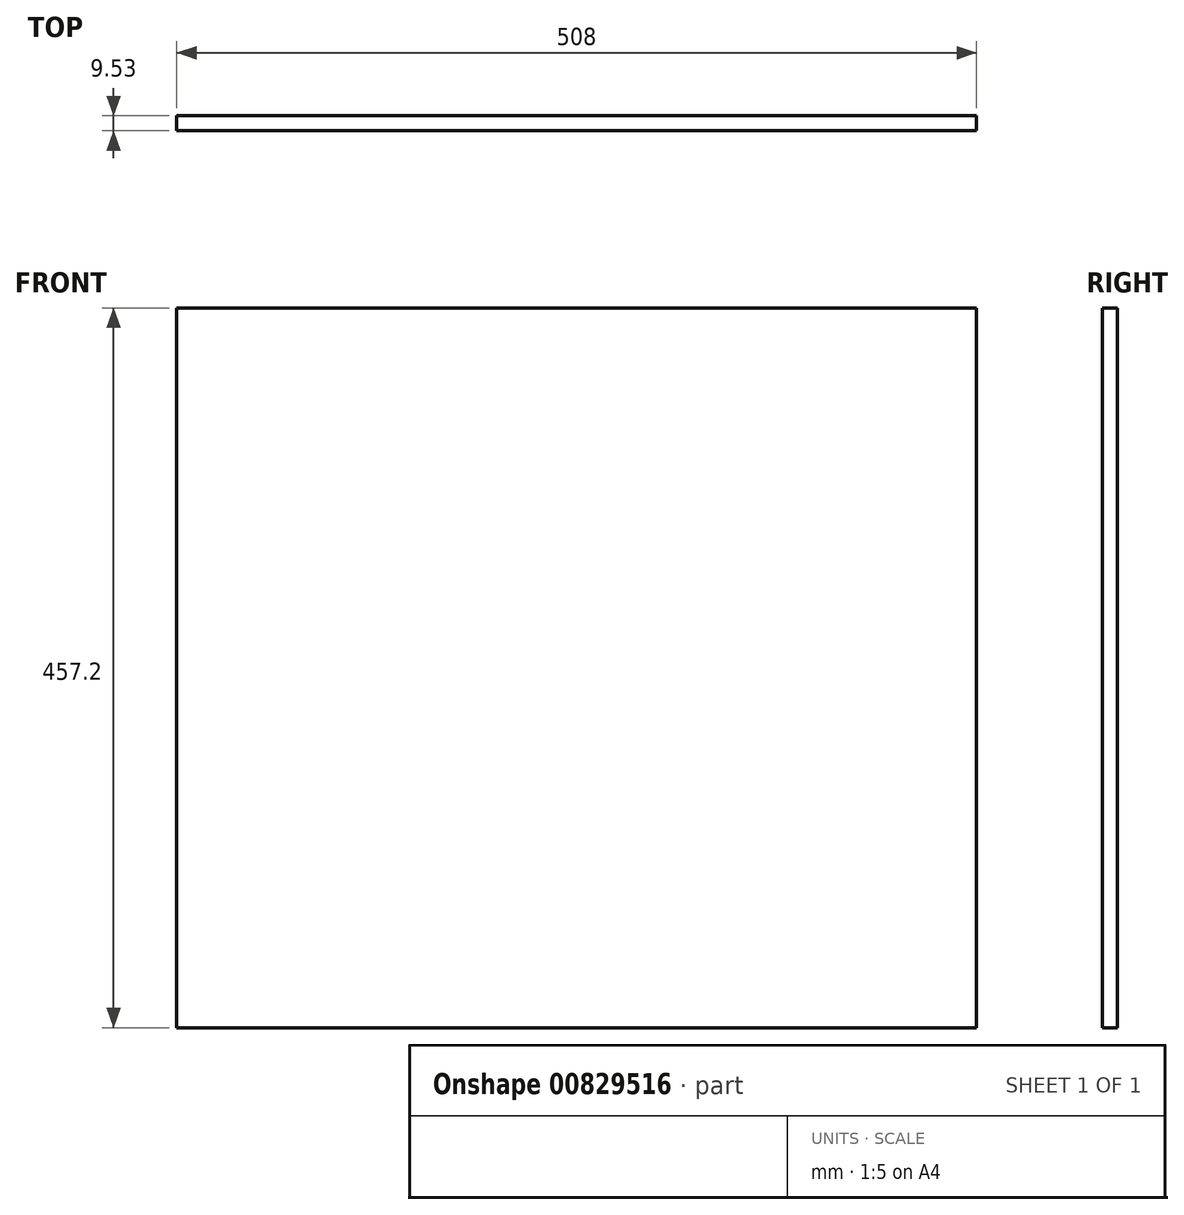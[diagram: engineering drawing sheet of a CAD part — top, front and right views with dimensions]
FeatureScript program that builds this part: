
annotation { "Feature Type Name" : "Feature", "Feature Type Description" : "" }
export const myFeature = defineFeature(function(context is Context, id is Id, definition is map)
    precondition{}
    {
        {
            var Q0;
            Q0=qCreatedBy(makeId("Front.planeOp"),FACE);
            var sketch = newSketch(context, id + "F0", { "sketchPlane" : qUnion([Q0])});
            skLineSegment(sketch, "E0.bottom", {"start": v(-254, -228.6) * mm, "end": v(254, -228.6) * mm});
            skLineSegment(sketch, "E0.top", {"start": v(-254, 228.6) * mm, "end": v(254, 228.6) * mm});
            skLineSegment(sketch, "E0.left", {"start": v(-254, -228.6) * mm, "end": v(-254, 228.6) * mm});
            skLineSegment(sketch, "E0.right", {"start": v(254, -228.6) * mm, "end": v(254, 228.6) * mm});
            skPoint(sketch, "E0.middle", {"position": v(0, 0) * mm});
            skSolve(sketch);
        }
        {
            var Q0;
            Q0 = qSketchRegion(id + "F0", true);
            extrude(context, id + "F1", {"entities" : qUnion([Q0]), "depth" : 9.52 * mm, "offsetDistance" : 25.4 * mm});
        }
    });
